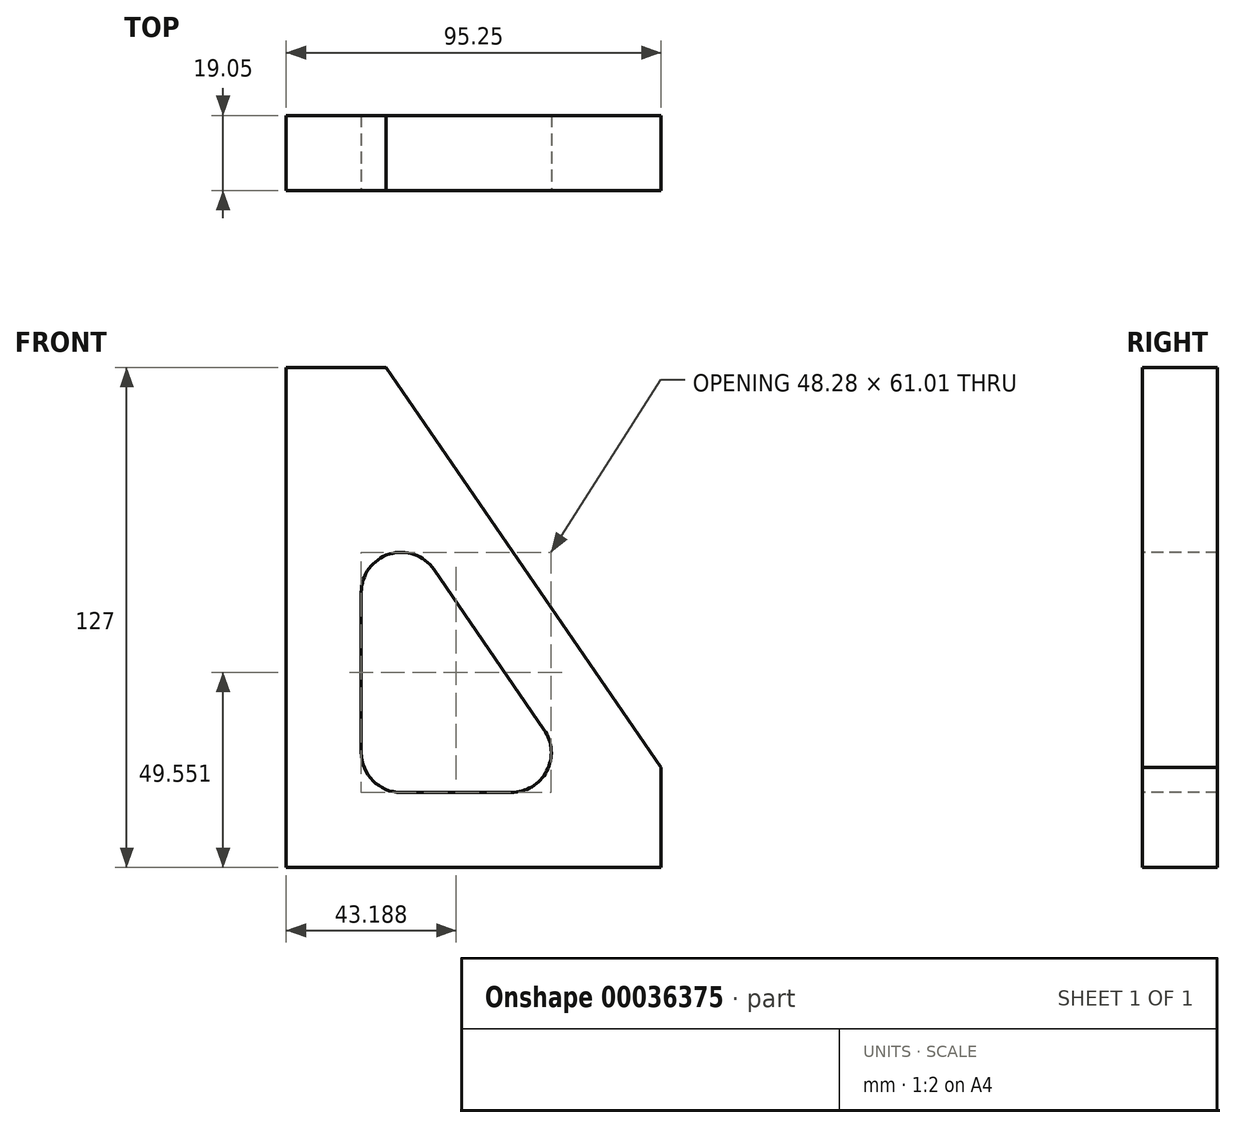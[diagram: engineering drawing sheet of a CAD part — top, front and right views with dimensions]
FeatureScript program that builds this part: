
annotation { "Feature Type Name" : "Feature", "Feature Type Description" : "" }
export const myFeature = defineFeature(function(context is Context, id is Id, definition is map)
    precondition{}
    {
        {
            var Q0;
            Q0=qCreatedBy(makeId("Front.planeOp"),FACE);
            var sketch = newSketch(context, id + "F0", { "sketchPlane" : qUnion([Q0])});
            skLineSegment(sketch, "E0", {"start": v(-25.4, 95.16) * mm, "end": v(-25.4, -31.84) * mm});
            skLineSegment(sketch, "E1", {"start": v(-25.4, -31.84) * mm, "end": v(69.85, -31.84) * mm});
            skLineSegment(sketch, "E2", {"start": v(69.85, -31.84) * mm, "end": v(69.85, -6.44) * mm});
            skLineSegment(sketch, "E3", {"start": v(69.85, -6.44) * mm, "end": v(0, 95.16) * mm});
            skLineSegment(sketch, "E4", {"start": v(-25.4, 95.16) * mm, "end": v(0, 95.16) * mm});
            skSolve(sketch);
        }
        {
            var Q0;
            Q0=makeQuery(id+"F0.imprint","IMPRINT",FACE,{"disambiguationData":[TD([[makeQuery(id+"F0.imprint","IMPRINT",EDGE,{"derivedFrom":sQuery(id+"F0.wireOp",EDGE,"E0")}),1.0]])]});
            var sketch = newSketch(context, id + "F1", { "sketchPlane" : qUnion([Q0])});
            skLineSegment(sketch, "E5", {"start": v(-6.35, 70.77) * mm, "end": v(-6.35, -12.8) * mm});
            skLineSegment(sketch, "E6", {"start": v(-6.35, -12.8) * mm, "end": v(51.1, -12.8) * mm});
            skLineSegment(sketch, "E7", {"start": v(-6.35, 70.77) * mm, "end": v(51.1, -12.8) * mm});
            skSolve(sketch);
        }
        {
            var Q0;
            Q0 = qSketchRegion(id + "F0", true);
            extrude(context, id + "F2", {"entities" : qUnion([Q0]), "oppositeDirection" : true, "depth" : 19.05 * mm});
        }
        {
            var Q0;
            Q0 = qSketchRegion(id + "F1", true);
            extrude(context, id + "F3", {"entities" : qUnion([Q0]), "operationType" : NewBodyOperationType.REMOVE, "endBound" : BoundingType.THROUGH_ALL, "oppositeDirection" : true, "depth" : 25.4 * mm});
        }
        {
            var Q0;
            Q0=makeQuery(id+"F3.boolean.opBoolean","COPY",EDGE,{"derivedFrom":makeQuery(id+"F3.opExtrude","SWEPT_EDGE",EDGE,{"disambiguationData":[OSD([sQuery(id+"F1.wireOp",EDGE,"E5"),sQuery(id+"F1.wireOp",EDGE,"E6")])]})});
            var Q1;
            Q1=makeQuery(id+"F3.boolean.opBoolean","COPY",EDGE,{"derivedFrom":makeQuery(id+"F3.opExtrude","SWEPT_EDGE",EDGE,{"disambiguationData":[OSD([sQuery(id+"F1.wireOp",EDGE,"E6"),sQuery(id+"F1.wireOp",EDGE,"E7")])]})});
            fillet(context, id + "F4", {"entities" : qUnion([Q0, Q1]), "radius" : 10.16 * mm, "tangentPropagation" : true, "allowEdgeOverflow" : false});
        }
        {
            var Q0;
            Q0=makeQuery(id+"F3.boolean.opBoolean","COPY",EDGE,{"derivedFrom":makeQuery(id+"F3.opExtrude","SWEPT_EDGE",EDGE,{"disambiguationData":[OSD([sQuery(id+"F1.wireOp",EDGE,"E5"),sQuery(id+"F1.wireOp",EDGE,"E7")])]})});
            fillet(context, id + "F5", {"entities" : qUnion([Q0]), "radius" : 10.16 * mm, "tangentPropagation" : true, "allowEdgeOverflow" : false});
        }
    });
